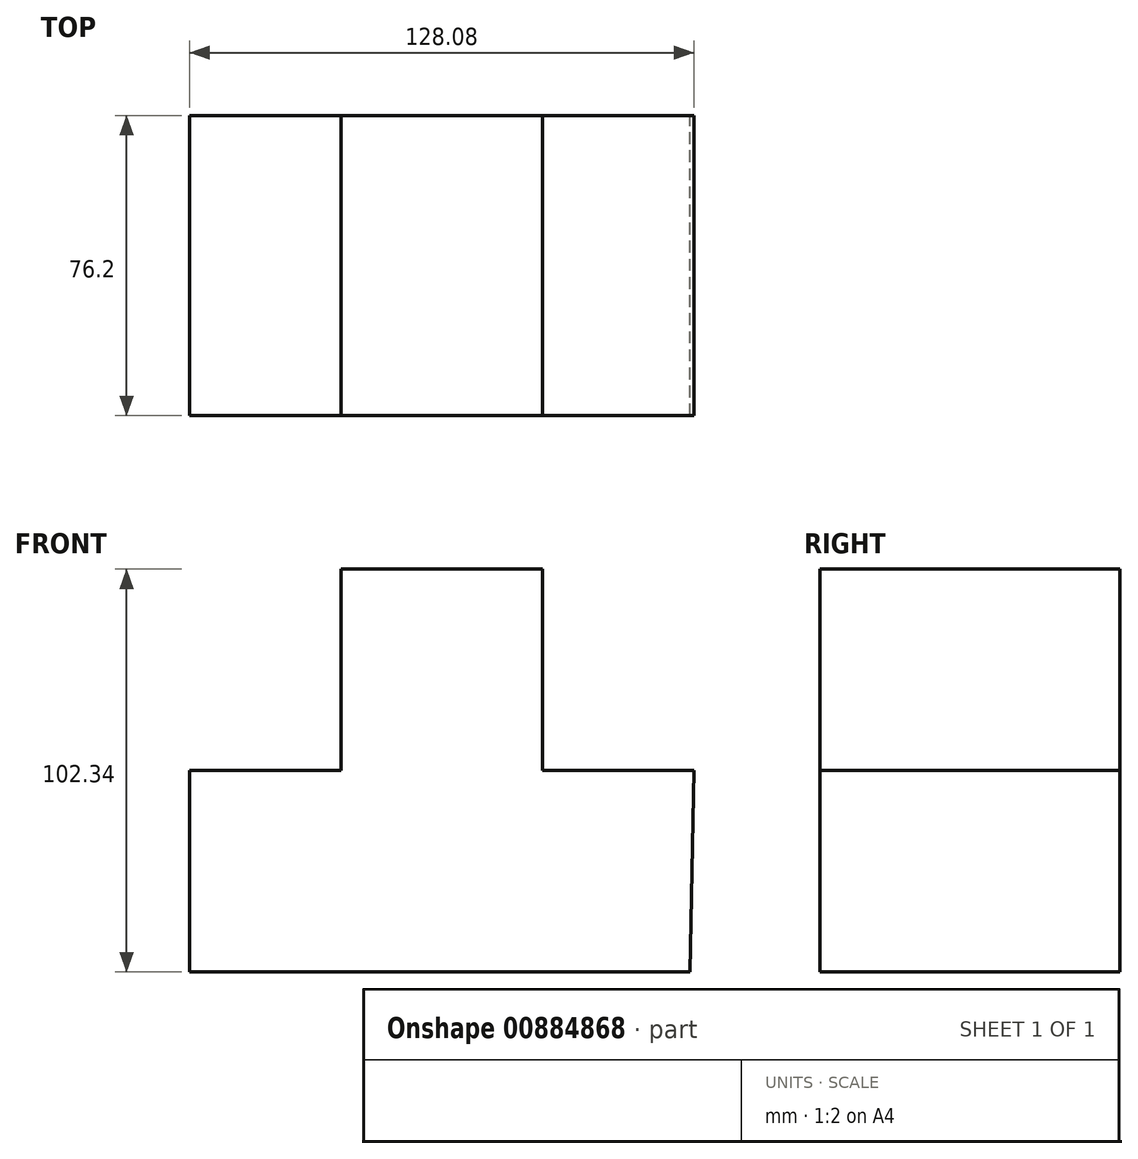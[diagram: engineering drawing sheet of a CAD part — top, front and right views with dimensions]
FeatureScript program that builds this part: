
annotation { "Feature Type Name" : "Feature", "Feature Type Description" : "" }
export const myFeature = defineFeature(function(context is Context, id is Id, definition is map)
    precondition{}
    {
        {
            var Q0;
            Q0=qCreatedBy(makeId("Front.planeOp"),FACE);
            var sketch = newSketch(context, id + "F0", { "sketchPlane" : qUnion([Q0])});
            skLineSegment(sketch, "E0", {"start": v(-64.66, 17.21) * mm, "end": v(-64.66, -33.96) * mm});
            skLineSegment(sketch, "E1", {"start": v(-64.66, -33.96) * mm, "end": v(62.49, -33.96) * mm});
            skLineSegment(sketch, "E2", {"start": v(-64.66, 17.21) * mm, "end": v(-26.2, 17.21) * mm});
            skLineSegment(sketch, "E3", {"start": v(-26.2, 17.21) * mm, "end": v(-26.2, 68.38) * mm});
            skLineSegment(sketch, "E4", {"start": v(-26.2, 68.38) * mm, "end": v(24.96, 68.38) * mm});
            skLineSegment(sketch, "E5", {"start": v(24.96, 68.38) * mm, "end": v(24.96, 17.21) * mm});
            skLineSegment(sketch, "E6", {"start": v(24.96, 17.21) * mm, "end": v(63.42, 17.21) * mm});
            skLineSegment(sketch, "E7", {"start": v(62.49, -33.96) * mm, "end": v(63.42, 17.21) * mm});
            skSolve(sketch);
        }
        {
            var Q0;
            Q0=qSketchRegion(id+"F0",true);
            extrude(context, id + "F1", {"entities" : qUnion([Q0]), "depth" : 76.2 * mm, "offsetDistance" : 25.4 * mm});
        }
    });
